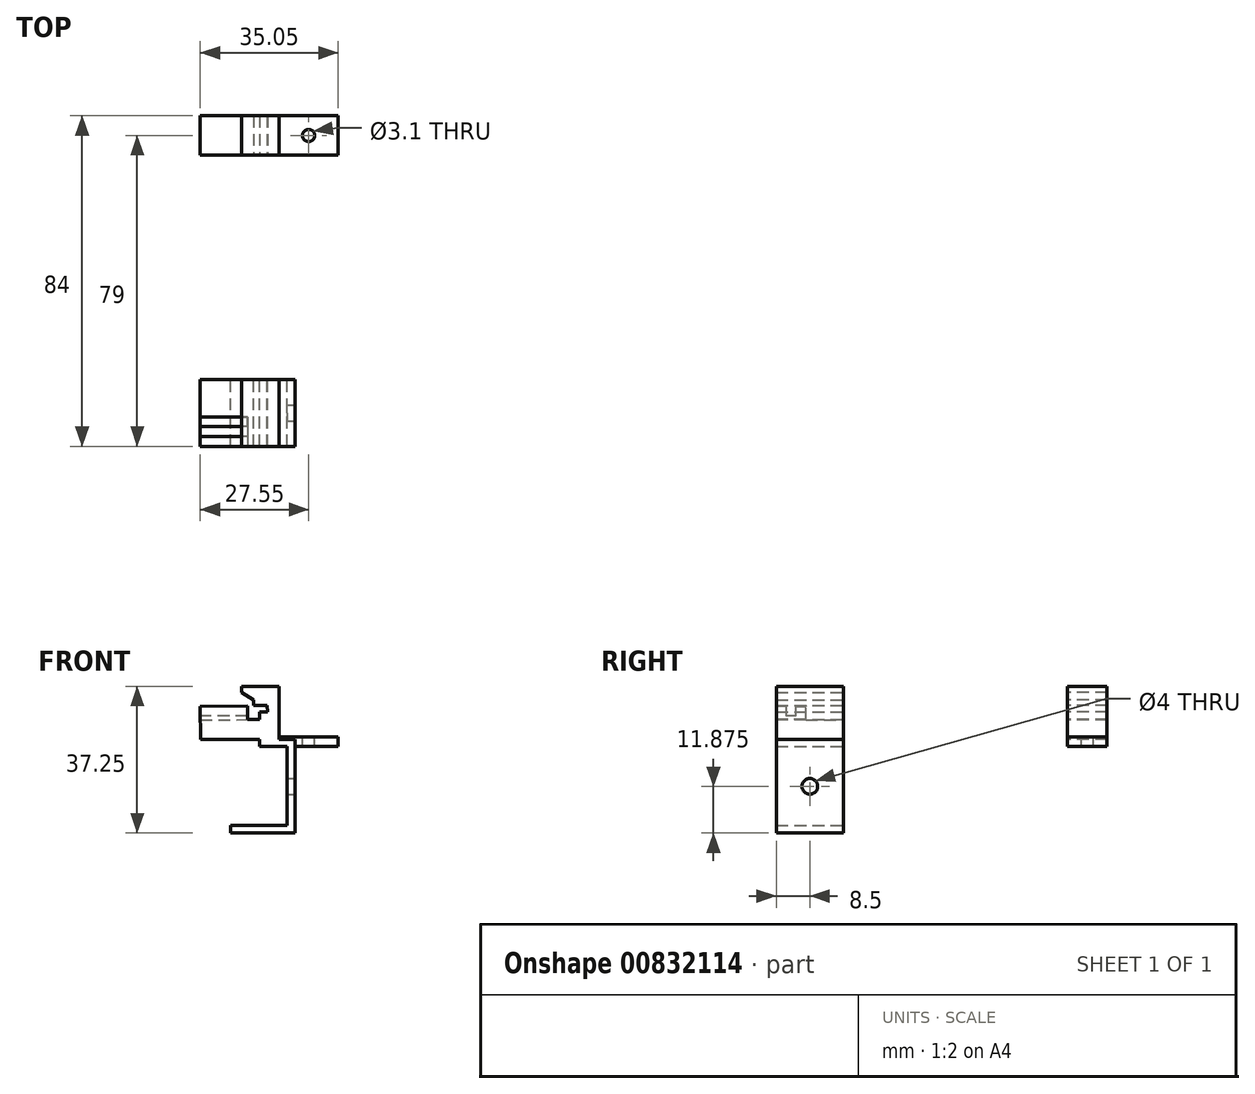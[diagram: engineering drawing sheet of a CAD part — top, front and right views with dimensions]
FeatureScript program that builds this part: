
annotation { "Feature Type Name" : "Feature", "Feature Type Description" : "" }
export const myFeature = defineFeature(function(context is Context, id is Id, definition is map)
    precondition{}
    {
        {
            var Q0;
            Q0=qCreatedBy(makeId("Front.planeOp"),FACE);
            var sketch = newSketch(context, id + "F0", { "sketchPlane" : qUnion([Q0])});
            skLineSegment(sketch, "E0.0", {"start": v(28, 1.75) * mm, "end": v(43, 1.75) * mm});
            skLineSegment(sketch, "E1.0", {"start": v(43, 1.75) * mm, "end": v(43, 0) * mm});
            skLineSegment(sketch, "E2", {"start": v(43, 0) * mm, "end": v(48, 0) * mm});
            skPoint(sketch, "E3.orphan", {"position": v(43, 9.75) * mm});
            skPoint(sketch, "E4.orphan", {"position": v(-43, 7.25) * mm});
            skPoint(sketch, "E5.orphan", {"position": v(-43, 1.75) * mm});
            skPoint(sketch, "E6.end.orphan", {"position": v(43, 7.25) * mm});
            skLineSegment(sketch, "E7", {"start": v(27.97, 6.75) * mm, "end": v(28, 1.75) * mm});
            skLineSegment(sketch, "E8", {"start": v(48, 13.75) * mm, "end": v(48, 1.75) * mm});
            skPoint(sketch, "E9.0.end.orphan", {"position": v(45, 9.75) * mm});
            skLineSegment(sketch, "E10.0", {"start": v(45, 9.75) * mm, "end": v(44, 9.75) * mm, "construction": true});
            skLineSegment(sketch, "E11.0", {"start": v(43, 8.5) * mm, "end": v(45, 9.75) * mm, "construction": true});
            skLineSegment(sketch, "E12", {"start": v(27.97, 6.75) * mm, "end": v(43, 6.84) * mm});
            skLineSegment(sketch, "E13.bottom", {"start": v(43, 0) * mm, "end": v(52, 0) * mm});
            skLineSegment(sketch, "E13.top", {"start": v(48, 1.75) * mm, "end": v(52, 1.75) * mm});
            skLineSegment(sketch, "E13.left", {"start": v(43, 0) * mm, "end": v(43, 1.75) * mm});
            skLineSegment(sketch, "E14.right", {"start": v(41.5, 11.88) * mm, "end": v(41.5, 10.45) * mm});
            skLineSegment(sketch, "E15", {"start": v(38.5, 13.75) * mm, "end": v(41.5, 11.88) * mm});
            skLineSegment(sketch, "E16", {"start": v(41.5, 10.45) * mm, "end": v(44.97, 10.45) * mm});
            skLineSegment(sketch, "E17", {"start": v(44.97, 10.45) * mm, "end": v(45, 8.79) * mm});
            skLineSegment(sketch, "E18", {"start": v(45, 8.79) * mm, "end": v(43, 8.75) * mm});
            skPoint(sketch, "E19.orphan", {"position": v(43, 10) * mm});
            skPoint(sketch, "E20.orphan", {"position": v(41.5, 10) * mm});
            skLineSegment(sketch, "E21", {"start": v(43, 8.75) * mm, "end": v(43, 6.84) * mm});
            skLineSegment(sketch, "E22.top", {"start": v(38.5, 15.25) * mm, "end": v(48, 15.25) * mm});
            skLineSegment(sketch, "E22.left", {"start": v(38.5, 13.75) * mm, "end": v(38.5, 15.25) * mm});
            skLineSegment(sketch, "E22.right", {"start": v(48, 13.75) * mm, "end": v(48, 15.25) * mm});
            skPoint(sketch, "E14.bottom.end.orphan", {"position": v(41.5, 13.75) * mm});
            skLineSegment(sketch, "E23.0", {"start": v(50, -20) * mm, "end": v(50, 0) * mm});
            skLineSegment(sketch, "E24.0", {"start": v(-50, -20) * mm, "end": v(50, -20) * mm});
            skLineSegment(sketch, "E25", {"start": v(48, 0) * mm, "end": v(50, 0) * mm});
            skLineSegment(sketch, "E26", {"start": v(50, -20) * mm, "end": v(35.7, -20) * mm});
            skLineSegment(sketch, "E27", {"start": v(35.7, -20) * mm, "end": v(35.7, -22) * mm});
            skLineSegment(sketch, "E28", {"start": v(35.7, -22) * mm, "end": v(52, -22) * mm});
            skLineSegment(sketch, "E29", {"start": v(52, -22) * mm, "end": v(52, 1.75) * mm});
            skPoint(sketch, "E13.right.end.orphan", {"position": v(63, 1.75) * mm});
            skSolve(sketch);
        }
        {
            var Q0;
            Q0=qSketchRegion(id+"F0",true);
            extrude(context, id + "F1", {"entities" : qUnion([Q0]), "depth" : 47 * mm});
        }
        {
            var Q0;
            Q0=qSketchRegion(id+"F0",true);
            extrude(context, id + "F2", {"entities" : qUnion([Q0]), "operationType" : NewBodyOperationType.REMOVE, "depth" : 30 * mm});
        }
        {
            var Q0;
            Q0=makeQuery(id+"F1.opExtrude","SWEPT_FACE",FACE,{"disambiguationData":[OSD([sQuery(id+"F0.wireOp",EDGE,"E7")])]});
            var sketch = newSketch(context, id + "F3", { "sketchPlane" : qUnion([Q0])});
            skPoint(sketch, "E30.right.end.orphan", {"position": v(-45, -81.5) * mm});
            skPoint(sketch, "E31.0.end.orphan", {"position": v(42, 12) * mm});
            skPoint(sketch, "E31.0.start.orphan", {"position": v(-42, 9.5) * mm});
            skPoint(sketch, "E32.0.end.orphan", {"position": v(-45, 12) * mm});
            skPoint(sketch, "E32.0.start.orphan", {"position": v(-45, 9.5) * mm});
            skPoint(sketch, "E33.0.end.orphan", {"position": v(-45, 9.08) * mm});
            skPoint(sketch, "E33.0.start.orphan", {"position": v(42, 7.08) * mm});
            skPoint(sketch, "E34.0.3.end.orphan", {"position": v(47, 6.58) * mm});
            skPoint(sketch, "E34.0.3.start.orphan", {"position": v(47, 6.58) * mm});
            skPoint(sketch, "E34.0.1.end.orphan", {"position": v(30, 6.58) * mm});
            skPoint(sketch, "E34.0.1.start.orphan", {"position": v(30, 6.58) * mm});
            skLineSegment(sketch, "E35.0", {"start": v(-45, 9.5) * mm, "end": v(-45, 12) * mm, "construction": true});
            skLineSegment(sketch, "E36.0", {"start": v(42, 8.25) * mm, "end": v(42, 9.58) * mm, "construction": true});
            skLineSegment(sketch, "E37.0", {"start": v(-45, 12) * mm, "end": v(-46, 12) * mm, "construction": true});
            skLineSegment(sketch, "E38.0", {"start": v(-45, 12) * mm, "end": v(-135, 12) * mm, "construction": true});
            skLineSegment(sketch, "E39.top", {"start": v(47, 5.94) * mm, "end": v(39.5, 5.94) * mm});
            skPoint(sketch, "E40.orphan", {"position": v(39.5, 7.08) * mm});
            skLineSegment(sketch, "E41", {"start": v(-45, 11.58) * mm, "end": v(-45, 9.08) * mm});
            skLineSegment(sketch, "E42", {"start": v(47, 10.08) * mm, "end": v(47, 5.94) * mm});
            skPoint(sketch, "E43.orphan", {"position": v(-42, 8.25) * mm});
            skLineSegment(sketch, "E44.right", {"start": v(47, 10.08) * mm, "end": v(47, 7.08) * mm});
            skPoint(sketch, "E45.orphan", {"position": v(45, 12) * mm});
            skPoint(sketch, "E46.0.start.orphan", {"position": v(45, 9.5) * mm});
            skLineSegment(sketch, "E47", {"start": v(44.5, 10.08) * mm, "end": v(44.5, 7.58) * mm});
            skLineSegment(sketch, "E48", {"start": v(42, 7.58) * mm, "end": v(42, 9.58) * mm});
            skLineSegment(sketch, "E49", {"start": v(39.5, 9.58) * mm, "end": v(39.5, 5.94) * mm});
            skLineSegment(sketch, "E50", {"start": v(42, 7.58) * mm, "end": v(44.5, 7.58) * mm});
            skLineSegment(sketch, "E51.top", {"start": v(42, 10.08) * mm, "end": v(39.5, 10.08) * mm});
            skLineSegment(sketch, "E51.left", {"start": v(42, 9.58) * mm, "end": v(42, 10.08) * mm});
            skLineSegment(sketch, "E51.right", {"start": v(39.5, 9.58) * mm, "end": v(39.5, 10.08) * mm});
            skLineSegment(sketch, "E52", {"start": v(44.5, 10.08) * mm, "end": v(47, 10.08) * mm});
            skSolve(sketch);
        }
        {
            var Q0;
            Q0=qSketchRegion(id+"F3",true);
            extrude(context, id + "F4", {"entities" : qUnion([Q0]), "operationType" : NewBodyOperationType.ADD, "oppositeDirection" : true, "depth" : 12 * mm});
        }
        {
            var Q0;
            Q0=makeQuery(id+"F1.opExtrude","SWEPT_FACE",FACE,{"disambiguationData":[OSD([sQuery(id+"F0.wireOp",EDGE,"E29")])]});
            var sketch = newSketch(context, id + "F5", { "sketchPlane" : qUnion([Q0])});
            skCircle(sketch, "E53", {"center": v(-38.5, -10.12) * mm, "radius": 2 * mm});
            skPoint(sketch, "E53.centerSnap0", {"position": v(-47, -10.12) * mm});
            skPoint(sketch, "E53.centerSnap1", {"position": v(-38.5, 1.75) * mm});
            skSolve(sketch);
        }
        {
            var Q0;
            Q0=qSketchRegion(id+"F5",true);
            extrude(context, id + "F6", {"entities" : qUnion([Q0]), "operationType" : NewBodyOperationType.REMOVE, "oppositeDirection" : true, "depth" : 3 * mm});
        }
        {
            var Q0;
            Q0=makeQuery(id+"F2.boolean.opBoolean","COPY",FACE,{"derivedFrom":makeQuery(id+"F2.opExtrude","CAP_FACE",FACE,{"disambiguationData":[OSD([sQuery(id+"F0.wireOp",EDGE,"E0.0"),sQuery(id+"F0.wireOp",EDGE,"E7"),sQuery(id+"F0.wireOp",EDGE,"E8"),sQuery(id+"F0.wireOp",EDGE,"E12"),sQuery(id+"F0.wireOp",EDGE,"E13.bottom"),sQuery(id+"F0.wireOp",EDGE,"E13.top"),sQuery(id+"F0.wireOp",EDGE,"E13.left"),sQuery(id+"F0.wireOp",EDGE,"E14.right"),sQuery(id+"F0.wireOp",EDGE,"E15"),sQuery(id+"F0.wireOp",EDGE,"E16"),sQuery(id+"F0.wireOp",EDGE,"E17"),sQuery(id+"F0.wireOp",EDGE,"E18"),sQuery(id+"F0.wireOp",EDGE,"E21"),sQuery(id+"F0.wireOp",EDGE,"E22.top"),sQuery(id+"F0.wireOp",EDGE,"E22.left"),sQuery(id+"F0.wireOp",EDGE,"E22.right"),sQuery(id+"F0.wireOp",EDGE,"E23.0"),sQuery(id+"F0.wireOp",EDGE,"E25"),sQuery(id+"F0.wireOp",EDGE,"E26"),sQuery(id+"F0.wireOp",EDGE,"E27"),sQuery(id+"F0.wireOp",EDGE,"E28"),sQuery(id+"F0.wireOp",EDGE,"E29")])],"isStart":false})});
            cPlane(context, id + "F7", {"entities" : qUnion([Q0]), "cplaneType" : CPlaneType.OFFSET, "offset" : 57 * mm, "width" : 150 * mm, "height" : 150 * mm});
        }
        {
            var Q0;
            Q0=qCreatedBy(id+"F7.planeOp",FACE);
            var sketch = newSketch(context, id + "F8", { "sketchPlane" : qUnion([Q0])});
            skLineSegment(sketch, "E54.0.0", {"start": v(-28, 1.75) * mm, "end": v(-27.97, 6.75) * mm});
            skLineSegment(sketch, "E54.0.1", {"start": v(-27.97, 6.75) * mm, "end": v(-43, 6.84) * mm});
            skLineSegment(sketch, "E54.0.2", {"start": v(-43, 6.84) * mm, "end": v(-43, 8.75) * mm});
            skLineSegment(sketch, "E54.0.3", {"start": v(-43, 8.75) * mm, "end": v(-45, 8.79) * mm});
            skLineSegment(sketch, "E54.0.4", {"start": v(-45, 8.79) * mm, "end": v(-44.97, 10.45) * mm});
            skLineSegment(sketch, "E54.0.5", {"start": v(-44.97, 10.45) * mm, "end": v(-41.5, 10.45) * mm});
            skLineSegment(sketch, "E54.0.6", {"start": v(-41.5, 10.45) * mm, "end": v(-41.5, 11.88) * mm});
            skLineSegment(sketch, "E54.0.7", {"start": v(-41.5, 11.88) * mm, "end": v(-38.5, 13.75) * mm});
            skLineSegment(sketch, "E54.0.8", {"start": v(-38.5, 13.75) * mm, "end": v(-38.5, 15.25) * mm});
            skLineSegment(sketch, "E54.0.9", {"start": v(-38.5, 15.25) * mm, "end": v(-48, 15.25) * mm});
            skLineSegment(sketch, "E54.0.10", {"start": v(-48, 15.25) * mm, "end": v(-48, 2.5) * mm});
            skLineSegment(sketch, "E54.0.18", {"start": v(-43, 0) * mm, "end": v(-43, 1.75) * mm});
            skLineSegment(sketch, "E54.0.19", {"start": v(-43, 1.75) * mm, "end": v(-28, 1.75) * mm});
            skPoint(sketch, "E54.0.16.end.orphan", {"position": v(-50, 0) * mm});
            skPoint(sketch, "E54.0.15.end.orphan", {"position": v(-50, -20) * mm});
            skPoint(sketch, "E54.0.13.start.orphan", {"position": v(-52, -22) * mm});
            skPoint(sketch, "E54.0.14.end.orphan", {"position": v(-35.7, -20) * mm});
            skPoint(sketch, "E54.0.14.start.orphan", {"position": v(-35.7, -22) * mm});
            skLineSegment(sketch, "E55.bottom", {"start": v(-43, 0) * mm, "end": v(-63, 0) * mm});
            skLineSegment(sketch, "E55.top", {"start": v(-48, 2.5) * mm, "end": v(-63, 2.5) * mm});
            skLineSegment(sketch, "E55.right", {"start": v(-63, 0) * mm, "end": v(-63, 2.5) * mm});
            skPoint(sketch, "E54.0.11.end.orphan", {"position": v(-52, 1.75) * mm});
            skPoint(sketch, "E56.orphan", {"position": v(-48, 1.75) * mm});
            skLineSegment(sketch, "E57.0", {"start": v(-39.97, 6.82) * mm, "end": v(-39.95, 10.32) * mm, "construction": true});
            skSolve(sketch);
        }
        {
            var Q0;
            Q0=qSketchRegion(id+"F8",true);
            extrude(context, id + "F9", {"entities" : qUnion([Q0]), "depth" : 10 * mm, "offsetDistance" : 25 * mm});
        }
        {
            var Q0;
            Q0=makeQuery(id+"F9.opExtrude","SWEPT_FACE",FACE,{"disambiguationData":[OSD([sQuery(id+"F8.wireOp",EDGE,"E55.top")])]});
            var sketch = newSketch(context, id + "F10", { "sketchPlane" : qUnion([Q0])});
            skLineSegment(sketch, "E58.0.0", {"start": v(48, 27) * mm, "end": v(63, 27) * mm, "construction": true});
            skLineSegment(sketch, "E58.0.1", {"start": v(63, 27) * mm, "end": v(63, 37) * mm, "construction": true});
            skLineSegment(sketch, "E58.0.2", {"start": v(63, 37) * mm, "end": v(48, 37) * mm, "construction": true});
            skLineSegment(sketch, "E58.0.3", {"start": v(48, 37) * mm, "end": v(48, 27) * mm, "construction": true});
            skPoint(sketch, "E59", {"position": v(55.5, 32) * mm});
            skPoint(sketch, "E59.positionSnap0", {"position": v(63, 32) * mm});
            skPoint(sketch, "E59.positionSnap1", {"position": v(55.5, 27) * mm});
            skCircle(sketch, "E60", {"center": v(55.5, 32) * mm, "radius": 1.55 * mm});
            skSolve(sketch);
        }
        {
            var Q0;
            Q0=qSketchRegion(id+"F10",true);
            extrude(context, id + "F11", {"entities" : qUnion([Q0]), "operationType" : NewBodyOperationType.REMOVE, "oppositeDirection" : true, "depth" : 25 * mm});
        }
    });
